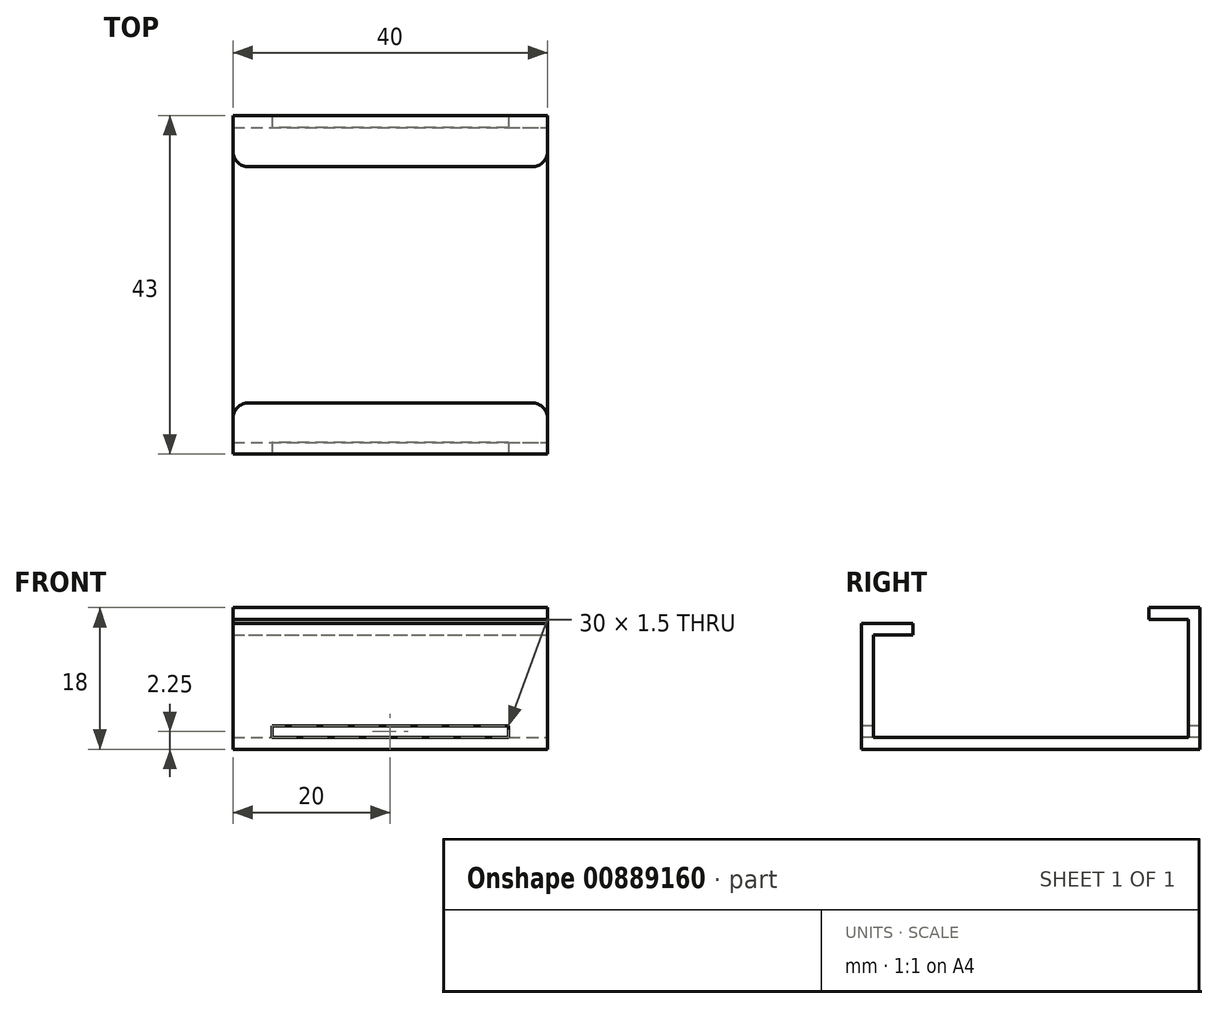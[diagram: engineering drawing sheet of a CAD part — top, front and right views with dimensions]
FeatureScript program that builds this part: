
annotation { "Feature Type Name" : "Feature", "Feature Type Description" : "" }
export const myFeature = defineFeature(function(context is Context, id is Id, definition is map)
    precondition{}
    {
        {
            var Q0;
            Q0=qCreatedBy(makeId("Top.planeOp"),FACE);
            var sketch = newSketch(context, id + "F0", { "sketchPlane" : qUnion([Q0])});
            skLineSegment(sketch, "E0.bottom", {"start": v(20, 21.5) * mm, "end": v(-20, 21.5) * mm});
            skLineSegment(sketch, "E0.top", {"start": v(20, -21.5) * mm, "end": v(-20, -21.5) * mm});
            skLineSegment(sketch, "E0.left", {"start": v(20, 21.5) * mm, "end": v(20, -21.5) * mm});
            skLineSegment(sketch, "E0.right", {"start": v(-20, 21.5) * mm, "end": v(-20, -21.5) * mm});
            skPoint(sketch, "E0.middle", {"position": v(0, 0) * mm});
            skSolve(sketch);
        }
        {
            var Q0;
            Q0=makeQuery(id+"F0.imprint","IMPRINT",FACE,{"disambiguationData":[TD([[makeQuery(id+"F0.imprint","IMPRINT",EDGE,{"derivedFrom":sQuery(id+"F0.wireOp",EDGE,"E0.bottom")}),1.0]])]});
            extrude(context, id + "F1", {"entities" : qUnion([Q0]), "depth" : 1.5 * mm, "offsetDistance" : 25 * mm});
        }
        {
            var Q0;
            Q0=makeQuery(id+"F1.opExtrude","CAP_FACE",FACE,{"disambiguationData":[OSD([sQuery(id+"F0.wireOp",EDGE,"E0.bottom"),sQuery(id+"F0.wireOp",EDGE,"E0.top"),sQuery(id+"F0.wireOp",EDGE,"E0.left"),sQuery(id+"F0.wireOp",EDGE,"E0.right")])],"isStart":false});
            var sketch = newSketch(context, id + "F2", { "sketchPlane" : qUnion([Q0])});
            skLineSegment(sketch, "E1.bottom", {"start": v(-20, -21.5) * mm, "end": v(20, -21.5) * mm});
            skLineSegment(sketch, "E1.top", {"start": v(-20, -20) * mm, "end": v(20, -20) * mm});
            skLineSegment(sketch, "E1.left", {"start": v(-20, -21.5) * mm, "end": v(-20, -20) * mm});
            skLineSegment(sketch, "E1.right", {"start": v(20, -21.5) * mm, "end": v(20, -20) * mm});
            skSolve(sketch);
        }
        {
            var Q0;
            Q0=makeQuery(id+"F2.imprint","IMPRINT",FACE,{"disambiguationData":[TD([[makeQuery(id+"F2.imprint","IMPRINT",EDGE,{"derivedFrom":sQuery(id+"F2.wireOp",EDGE,"E1.bottom")}),-1.0]])]});
            extrude(context, id + "F3", {"entities" : qUnion([Q0]), "operationType" : NewBodyOperationType.ADD, "depth" : 14.5 * mm, "offsetDistance" : 25 * mm});
        }
        {
            var Q0;
            Q0=makeQuery(id+"F1.opExtrude","CAP_FACE",FACE,{"disambiguationData":[OSD([sQuery(id+"F0.wireOp",EDGE,"E0.bottom"),sQuery(id+"F0.wireOp",EDGE,"E0.top"),sQuery(id+"F0.wireOp",EDGE,"E0.left"),sQuery(id+"F0.wireOp",EDGE,"E0.right")])],"isStart":false});
            var sketch = newSketch(context, id + "F4", { "sketchPlane" : qUnion([Q0])});
            skLineSegment(sketch, "E2.bottom", {"start": v(-20, 21.5) * mm, "end": v(20, 21.5) * mm});
            skLineSegment(sketch, "E2.top", {"start": v(-20, 20) * mm, "end": v(20, 20) * mm});
            skLineSegment(sketch, "E2.left", {"start": v(-20, 21.5) * mm, "end": v(-20, 20) * mm});
            skLineSegment(sketch, "E2.right", {"start": v(20, 21.5) * mm, "end": v(20, 20) * mm});
            skSolve(sketch);
        }
        {
            var Q0;
            Q0 = qSketchRegion(id + "F4", true);
            extrude(context, id + "F5", {"entities" : qUnion([Q0]), "operationType" : NewBodyOperationType.ADD, "depth" : 16.5 * mm, "offsetDistance" : 25 * mm});
        }
        {
            var Q0;
            Q0=makeQuery(id+"F5.opExtrude","SWEPT_FACE",FACE,{"disambiguationData":[OSD([sQuery(id+"F4.wireOp",EDGE,"E2.top")])]});
            var sketch = newSketch(context, id + "F6", { "sketchPlane" : qUnion([Q0])});
            skLineSegment(sketch, "E3.bottom", {"start": v(-20, 18) * mm, "end": v(20, 18) * mm});
            skLineSegment(sketch, "E3.top", {"start": v(-20, 16.5) * mm, "end": v(20, 16.5) * mm});
            skLineSegment(sketch, "E3.left", {"start": v(-20, 18) * mm, "end": v(-20, 16.5) * mm});
            skLineSegment(sketch, "E3.right", {"start": v(20, 18) * mm, "end": v(20, 16.5) * mm});
            skSolve(sketch);
        }
        {
            var Q0;
            Q0 = qSketchRegion(id + "F6", true);
            extrude(context, id + "F7", {"entities" : qUnion([Q0]), "operationType" : NewBodyOperationType.ADD, "depth" : 5 * mm, "offsetDistance" : 25 * mm});
        }
        {
            var Q0;
            Q0=makeQuery(id+"F3.opExtrude","SWEPT_FACE",FACE,{"disambiguationData":[OSD([sQuery(id+"F2.wireOp",EDGE,"E1.top")])]});
            var sketch = newSketch(context, id + "F8", { "sketchPlane" : qUnion([Q0])});
            skLineSegment(sketch, "E4.bottom", {"start": v(20, 16) * mm, "end": v(-20, 16) * mm});
            skLineSegment(sketch, "E4.top", {"start": v(20, 14.5) * mm, "end": v(-20, 14.5) * mm});
            skLineSegment(sketch, "E4.left", {"start": v(20, 16) * mm, "end": v(20, 14.5) * mm});
            skLineSegment(sketch, "E4.right", {"start": v(-20, 16) * mm, "end": v(-20, 14.5) * mm});
            skSolve(sketch);
        }
        {
            var Q0;
            Q0 = qSketchRegion(id + "F8", true);
            extrude(context, id + "F9", {"entities" : qUnion([Q0]), "operationType" : NewBodyOperationType.ADD, "depth" : 5 * mm, "offsetDistance" : 25 * mm});
        }
        {
            var Q0;
            Q0=makeQuery(id+"F3.boolean.opBoolean","MERGE",FACE,{"derivedFrom":[makeQuery(id+"F1.opExtrude","SWEPT_FACE",FACE,{"disambiguationData":[OSD([sQuery(id+"F0.wireOp",EDGE,"E0.top")])]}),makeQuery(id+"F3.opExtrude","SWEPT_FACE",FACE,{"disambiguationData":[OSD([sQuery(id+"F2.wireOp",EDGE,"E1.bottom")])]})]});
            var sketch = newSketch(context, id + "F10", { "sketchPlane" : qUnion([Q0])});
            skLineSegment(sketch, "E5.bottom", {"start": v(-15, 1.5) * mm, "end": v(15, 1.5) * mm});
            skLineSegment(sketch, "E5.top", {"start": v(-15, 3) * mm, "end": v(15, 3) * mm});
            skLineSegment(sketch, "E5.left", {"start": v(-15, 1.5) * mm, "end": v(-15, 3) * mm});
            skLineSegment(sketch, "E5.right", {"start": v(15, 1.5) * mm, "end": v(15, 3) * mm});
            skSolve(sketch);
        }
        {
            var Q0;
            Q0 = qSketchRegion(id + "F10", true);
            extrude(context, id + "F11", {"entities" : qUnion([Q0]), "operationType" : NewBodyOperationType.REMOVE, "oppositeDirection" : true, "depth" : 44 * mm, "offsetDistance" : 25 * mm});
        }
        {
            var Q0;
            Q0=makeQuery(id+"F7.opExtrude","CAP_EDGE",EDGE,{"disambiguationData":[OSD([sQuery(id+"F6.wireOp",EDGE,"E3.right")])],"isStart":false});
            var Q1;
            Q1=makeQuery(id+"F9.opExtrude","CAP_EDGE",EDGE,{"disambiguationData":[OSD([sQuery(id+"F8.wireOp",EDGE,"E4.right")])],"isStart":false});
            var Q2;
            Q2=makeQuery(id+"F7.opExtrude","CAP_EDGE",EDGE,{"disambiguationData":[OSD([sQuery(id+"F6.wireOp",EDGE,"E3.left")])],"isStart":false});
            var Q3;
            Q3=makeQuery(id+"F9.opExtrude","CAP_EDGE",EDGE,{"disambiguationData":[OSD([sQuery(id+"F8.wireOp",EDGE,"E4.left")])],"isStart":false});
            fillet(context, id + "F12", {"entities" : qUnion([Q0, Q1, Q2, Q3]), "radius" : 2 * mm, "tangentPropagation" : true, "allowEdgeOverflow" : false});
        }
    });
